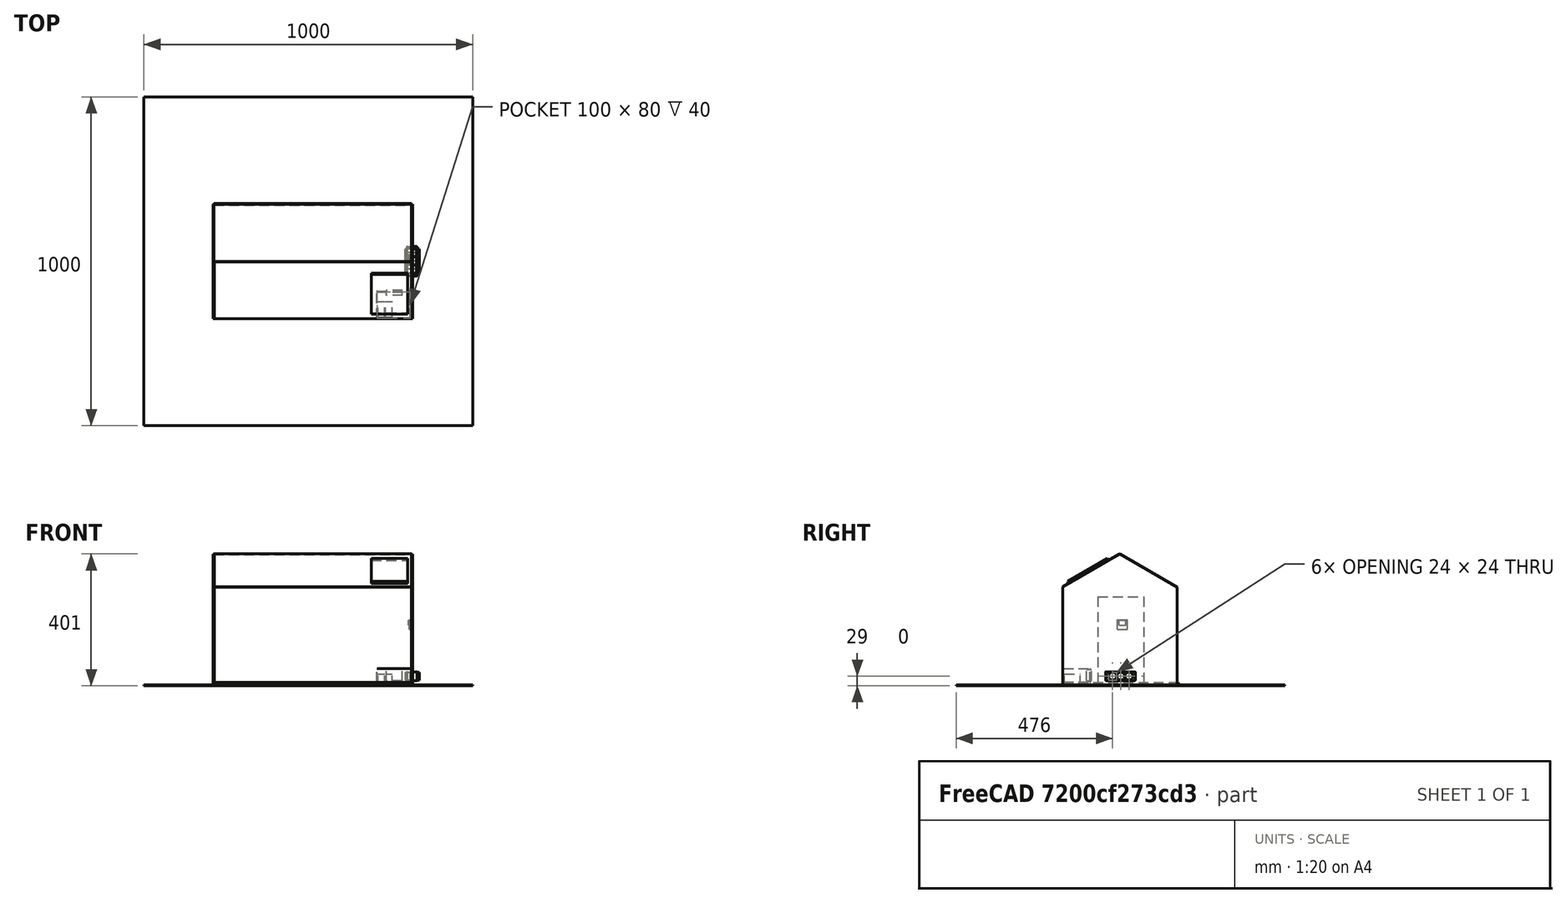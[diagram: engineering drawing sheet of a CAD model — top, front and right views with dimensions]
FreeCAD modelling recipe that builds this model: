
FCSTD DOCUMENT  (FreeCAD 0.20R29177 +233 (Git))
Label: green house
License: All rights reserved
LicenseURL: http://en.wikipedia.org/wiki/All_rights_reserved
objects: Part::Box×30, Part::Cylinder×6, Part::Cut×5, Part::MultiFuse×4, Part::Thickness×2, App::DocumentObjectGroup×2
note: 47 computed .brp shape members not serialized (recipe doc carries the construction recipe); baked Part::Feature solids carry a one-line shape summary decoded from their .brp

FEATURE [Part::Box] Box  label="Glass"
  AttacherType = Attacher::AttachEngine3D
  Height = 300
  Length = 600
  Width = 2
FEATURE [Part::Box] Box001  label="Glass001"
  AttacherType = Attacher::AttachEngine3D
  Height = 300
  Length = 600
  Placement = pos=(0,346,0) rot=(0,0,1;0rad)
  Width = 2
FEATURE [Part::Box] Box002  label="Glass002"
  AttacherType = Attacher::AttachEngine3D
  Height = 200
  Length = 600
  Placement = pos=(0,0,301) rot=(-1,0,0;1.0472rad)
  Width = 2
FEATURE [Part::Box] Box003  label="Glass003"
  AttacherType = Attacher::AttachEngine3D
  Height = 200
  Length = 600
  Placement = pos=(0,347.144,298.608) rot=(1,0,0;1.0472rad)
  Width = 2
FEATURE [Part::Box] Box004  label="Glass004"
  AttacherType = Attacher::AttachEngine3D
  Height = 400
  Length = 348
  Placement = pos=(605,-2e-15,0) rot=(0,0,1;1.5708rad)
  Width = 4
FEATURE [Part::Box] Box005  label="Glass cut "
  AttacherType = Attacher::AttachEngine3D
  Height = 87
  Length = 18
  Placement = pos=(598,-0.25833,301.447) rot=(1,0,0;0.523599rad)
  Width = 200
FEATURE [Part::Cut] Cut
  Base = -> Box004
  Tool = -> Box005
FEATURE [Part::Box] Box006  label="Glass cut 001"
  AttacherType = Attacher::AttachEngine3D
  Height = 87
  Length = 18
  Placement = pos=(598,174.529,399.72) rot=(-1,0,0;0.523599rad)
  Width = 200
FEATURE [Part::Cut] Cut001  label="Glass sides"
  Base = -> Cut
  Tool = -> Box006
FEATURE [Part::Box] Box007  label="Glass005"
  AttacherType = Attacher::AttachEngine3D
  Height = 400
  Length = 348
  Placement = pos=(605,-2e-15,0) rot=(0,0,1;1.5708rad)
  Width = 4
FEATURE [Part::Box] Box008  label="Glass cut 002"
  AttacherType = Attacher::AttachEngine3D
  Height = 87
  Length = 18
  Placement = pos=(598,-0.25833,301.447) rot=(1,0,0;0.523599rad)
  Width = 200
FEATURE [Part::Box] Box009  label="Glass cut 003"
  AttacherType = Attacher::AttachEngine3D
  Height = 87
  Length = 18
  Placement = pos=(598,174.529,399.72) rot=(-1,0,0;0.523599rad)
  Width = 200
FEATURE [Part::Cut] Cut002
  Base = -> Box007
  Tool = -> Box008
FEATURE [Part::Cut] Cut003  label="Glass sides001"
  Base = -> Cut002
  Placement = pos=(-604,0,0) rot=(0,0,1;0rad)
  Tool = -> Box009
FEATURE [Part::Box] Box010  label="Controller"
  AttacherType = Attacher::AttachEngine3D
  Height = 30
  Length = 10
  Placement = pos=(594,166,171) rot=(0,0,1;0rad)
  Width = 30
FEATURE [Part::Box] Box011  label="Display"
  AttacherType = Attacher::AttachEngine3D
  Height = 15
  Length = 10
  Placement = pos=(592,171,184) rot=(0,0,1;0rad)
  Width = 20
FEATURE [Part::Box] Box012  label="Ground"
  AttacherType = Attacher::AttachEngine3D
  Height = 3
  Length = 1000
  Placement = pos=(-213,-325,0) rot=(0,0,1;0rad)
  Width = 1000
FEATURE [Part::Box] Box013  label="Door"
  AttacherType = Attacher::AttachEngine3D
  Height = 270
  Length = 10
  Placement = pos=(-5,106,0) rot=(0,0,1;0rad)
  Width = 140
FEATURE [Part::Cut] Cut004
  Base = -> Cut003
  Tool = -> Box013
FEATURE [Part::Box] Box014  label="Battery bank "
  AttacherType = Attacher::AttachEngine3D
  Height = 40
  Length = 100
  Placement = pos=(544,2,0) rot=(0,0,1;0rad)
  Width = 80
FEATURE [Part::Thickness] Thickness  label="Power & logic bank"
  Faces = -> Box014 [Face6]
  Intersection = false
  Join = 0
  Mode = 0
  Placement = pos=(-47,0,12) rot=(0,0,1;0rad)
  SelfIntersection = false
  Value = 2
FEATURE [Part::Box] Box015  label="Battery"
  AttacherType = Attacher::AttachEngine3D
  Height = 35
  Length = 20
  Placement = pos=(499,5,0) rot=(0,0,1;0rad)
  Width = 48
FEATURE [Part::Box] Box016  label="Battery001"
  AttacherType = Attacher::AttachEngine3D
  Height = 35
  Length = 20
  Placement = pos=(522,5,0) rot=(0,0,1;0rad)
  Width = 48
FEATURE [Part::Box] Box017  label="Solar panel"
  AttacherType = Attacher::AttachEngine3D
  Height = 140
  Length = 110
  Placement = pos=(479,14.1917,317.419) rot=(-1,0,0;1.0472rad)
  Width = 7
FEATURE [Part::Box] Box018  label="Floor"
  AttacherType = Attacher::AttachEngine3D
  Height = 10
  Length = 600
  Width = 351
FEATURE [Part::Box] Box020  label="Cube"
  AttacherType = Attacher::AttachEngine3D
  Height = 1
  Length = 25
  Width = 25
FEATURE [Part::Box] Box021  label="Cube001"
  AttacherType = Attacher::AttachEngine3D
  Height = 1
  Length = 25
  Placement = pos=(0,0,1) rot=(0,0,1;0rad)
  Width = 25
FEATURE [Part::Box] Box022  label="Cube002"
  AttacherType = Attacher::AttachEngine3D
  Height = 2
  Length = 25
  Placement = pos=(0,0,2) rot=(0,0,1;0rad)
  Width = 25
FEATURE [Part::Box] Box023  label="Cube003"
  AttacherType = Attacher::AttachEngine3D
  Height = 1
  Length = 25
  Width = 25
FEATURE [Part::Box] Box024  label="Cube004"
  AttacherType = Attacher::AttachEngine3D
  Height = 1
  Length = 25
  Placement = pos=(0,0,1) rot=(0,0,1;0rad)
  Width = 25
FEATURE [Part::Box] Box025  label="Cube005"
  AttacherType = Attacher::AttachEngine3D
  Height = 2
  Length = 25
  Placement = pos=(0,0,2) rot=(0,0,1;0rad)
  Width = 25
FEATURE [Part::Box] Box026  label="Cube006"
  AttacherType = Attacher::AttachEngine3D
  Height = 1
  Length = 25
  Width = 25
FEATURE [Part::Box] Box027  label="Cube007"
  AttacherType = Attacher::AttachEngine3D
  Height = 1
  Length = 25
  Placement = pos=(0,0,1) rot=(0,0,1;0rad)
  Width = 25
FEATURE [Part::Box] Box028  label="Cube008"
  AttacherType = Attacher::AttachEngine3D
  Height = 2
  Length = 25
  Placement = pos=(0,0,2) rot=(0,0,1;0rad)
  Width = 25
FEATURE [Part::Box] Box029  label="Cube009"
  AttacherType = Attacher::AttachEngine3D
  Height = 28
  Length = 25
  Placement = pos=(0,-55,-13) rot=(0,0,1;0rad)
  Width = 86
FEATURE [Part::Cylinder] Cylinder
  Angle = 360
  AttacherType = Attacher::AttachEngine3D
  FirstAngle = 0
  Height = 20
  Placement = pos=(12,12,4) rot=(0,0,1;0rad)
  Radius = 12
  SecondAngle = 0
FEATURE [Part::Cylinder] Cylinder001
  Angle = 360
  AttacherType = Attacher::AttachEngine3D
  FirstAngle = 0
  Height = 20
  Placement = pos=(12,12,-20) rot=(0,0,1;0rad)
  Radius = 12
  SecondAngle = 0
FEATURE [Part::Cylinder] Cylinder002
  Angle = 360
  AttacherType = Attacher::AttachEngine3D
  FirstAngle = 0
  Height = 20
  Placement = pos=(12,12,4) rot=(0,0,1;0rad)
  Radius = 12
  SecondAngle = 0
FEATURE [Part::Cylinder] Cylinder003
  Angle = 360
  AttacherType = Attacher::AttachEngine3D
  FirstAngle = 0
  Height = 20
  Placement = pos=(12,12,-20) rot=(0,0,1;0rad)
  Radius = 12
  SecondAngle = 0
FEATURE [Part::Cylinder] Cylinder004
  Angle = 360
  AttacherType = Attacher::AttachEngine3D
  FirstAngle = 0
  Height = 20
  Placement = pos=(12,12,4) rot=(0,0,1;0rad)
  Radius = 12
  SecondAngle = 0
FEATURE [Part::Cylinder] Cylinder005
  Angle = 360
  AttacherType = Attacher::AttachEngine3D
  FirstAngle = 0
  Height = 20
  Placement = pos=(12,12,-20) rot=(0,0,1;0rad)
  Radius = 12
  SecondAngle = 0
FEATURE [Part::MultiFuse] Fusion  label="jet"
  Shapes = -> [Box020,Box021,Box022,Cylinder,Cylinder001]
FEATURE [Part::MultiFuse] Fusion001  label="jet001"
  Placement = pos=(0,-25,0) rot=(0,0,1;0rad)
  Shapes = -> [Box023,Box024,Box025,Cylinder002,Cylinder003]
FEATURE [Part::MultiFuse] Fusion002  label="jet002"
  Placement = pos=(0,-50,0) rot=(0,0,1;0rad)
  Shapes = -> [Box026,Box027,Box028,Cylinder004,Cylinder005]
FEATURE [Part::Thickness] Thickness001
  Faces = -> Box029 [Face2]
  Intersection = false
  Join = 0
  Mode = 0
  SelfIntersection = false
  Value = 2
FEATURE [Part::MultiFuse] Fusion003  label="Heater \ Cooler"
  Placement = pos=(601,163,17) rot=(0.707107,0,0.707107;3.14159rad)
  Shapes = -> [Thickness001,Fusion002,Fusion001,Fusion]
FEATURE [Part::Box] Box030  label="Charge controller"
  AttacherType = Attacher::AttachEngine3D
  Height = 35
  Length = 15
  Placement = pos=(573,72,15) rot=(0,0,1;1.5708rad)
  Width = 48
FEATURE [App::DocumentObjectGroup] Group  label="Green House"
  Group = -> [Box003,Box002,Box001,Box,Cut001,Cut004]
FEATURE [App::DocumentObjectGroup] Group001  label="Heating system"
  Group = -> [Box010,Box011,Thickness,Box015,Box016,Box017,Fusion003,Box030]
